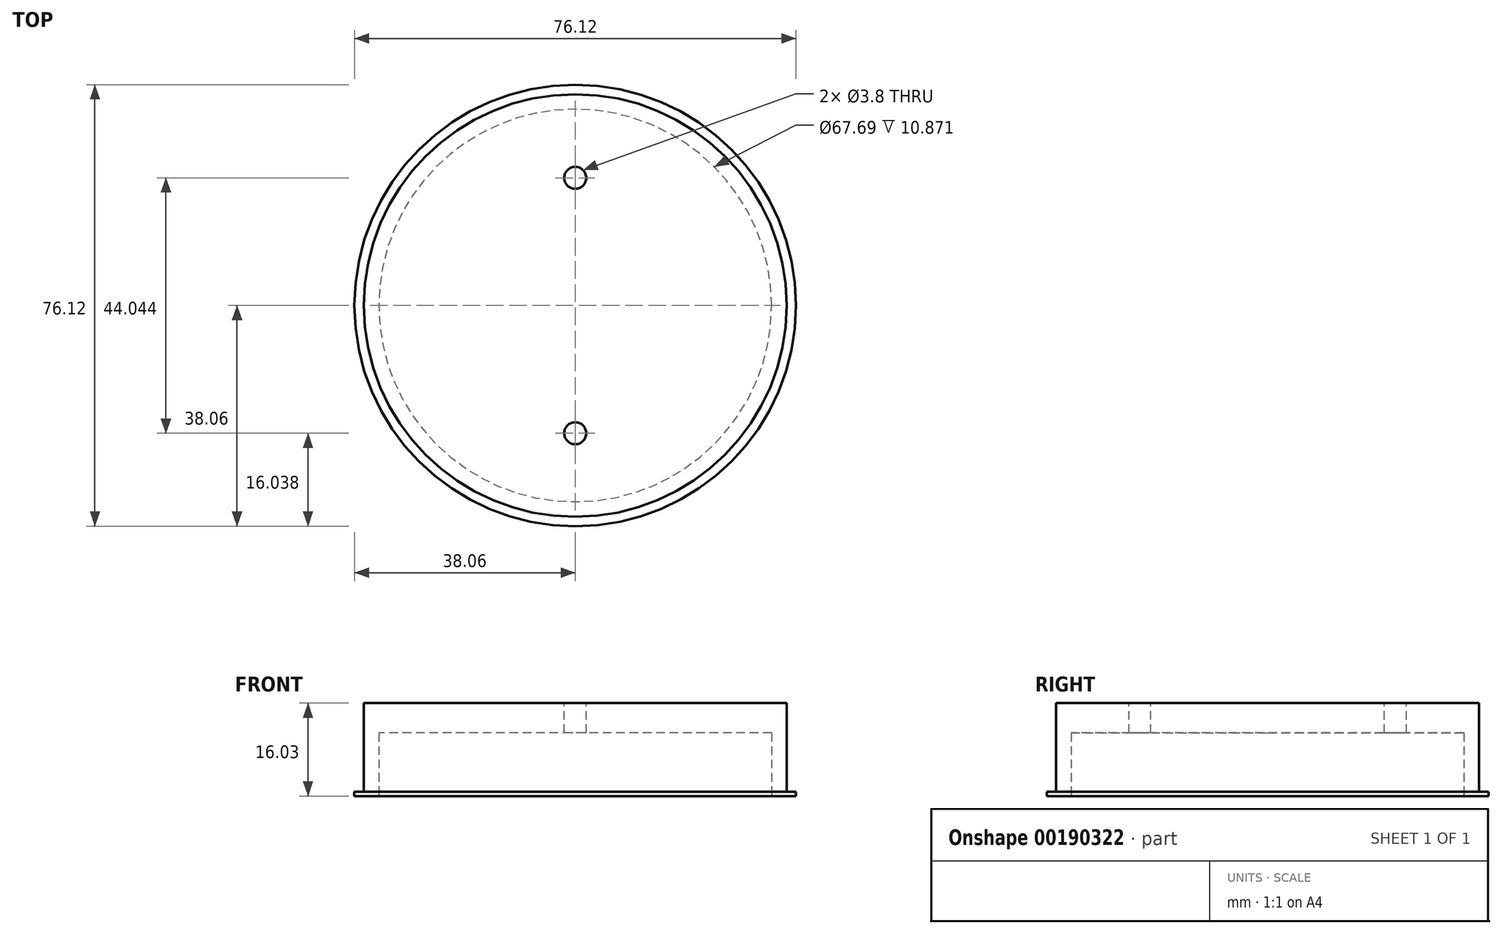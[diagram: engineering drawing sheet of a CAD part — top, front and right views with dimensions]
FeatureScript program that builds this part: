
annotation { "Feature Type Name" : "Feature", "Feature Type Description" : "" }
export const myFeature = defineFeature(function(context is Context, id is Id, definition is map)
    precondition{}
    {
        {
            var Q0;
            Q0=qCreatedBy(makeId("Top.planeOp"),FACE);
            var sketch = newSketch(context, id + "F0", { "sketchPlane" : qUnion([Q0])});
            skCircle(sketch, "E0", {"center": v(0, 0) * mm, "radius": 38.06 * mm});
            skCircle(sketch, "E1", {"center": v(0, 0) * mm, "radius": 36.44 * mm});
            skCircle(sketch, "E2", {"center": v(0, 0) * mm, "radius": 33.85 * mm});
            skSolve(sketch);
        }
        {
            var Q0;
            Q0=makeQuery(id+"F0.imprint","IMPRINT",FACE,{"disambiguationData":[TD([[makeQuery(id+"F0.imprint","IMPRINT",EDGE,{"derivedFrom":sQuery(id+"F0.wireOp",EDGE,"E0")}),1.0]])]});
            extrude(context, id + "F1", {"entities" : qUnion([Q0]), "depth" : 0.71 * mm});
        }
        {
            var Q0;
            Q0=makeQuery(id+"F0.imprint","IMPRINT",FACE,{"disambiguationData":[TD([[makeQuery(id+"F0.imprint","IMPRINT",EDGE,{"derivedFrom":sQuery(id+"F0.wireOp",EDGE,"E1")}),1.0]])]});
            var Q1;
            Q1=makeQuery(id+"F0.imprint","IMPRINT",FACE,{"disambiguationData":[TD([[makeQuery(id+"F0.imprint","IMPRINT",EDGE,{"derivedFrom":sQuery(id+"F0.wireOp",EDGE,"E2")}),1.0]])]});
            extrude(context, id + "F2", {"entities" : qUnion([Q0, Q1]), "operationType" : NewBodyOperationType.ADD, "depth" : 16.03 * mm});
        }
        {
            var Q0;
            Q0=makeQuery(id+"F0.imprint","IMPRINT",FACE,{"disambiguationData":[TD([[makeQuery(id+"F0.imprint","IMPRINT",EDGE,{"derivedFrom":sQuery(id+"F0.wireOp",EDGE,"E2")}),1.0]])]});
            extrude(context, id + "F3", {"entities" : qUnion([Q0]), "operationType" : NewBodyOperationType.REMOVE, "depth" : 10.87 * mm});
        }
        {
            var Q0;
            Q0=makeQuery(id+"F0.imprint","IMPRINT",FACE,{"disambiguationData":[TD([[makeQuery(id+"F0.imprint","IMPRINT",EDGE,{"derivedFrom":sQuery(id+"F0.wireOp",EDGE,"E2")}),1.0]])]});
            var sketch = newSketch(context, id + "F4", { "sketchPlane" : qUnion([Q0])});
            skLineSegment(sketch, "E3", {"start": v(-6.96, -22.02) * mm, "end": v(11.6, -22.02) * mm});
            skLineSegment(sketch, "E4", {"start": v(-5.97, 22.02) * mm, "end": v(8.6, 22.02) * mm});
            skLineSegment(sketch, "E5", {"start": v(0, 0) * mm, "end": v(0, 22.02) * mm});
            skLineSegment(sketch, "E6", {"start": v(0, 0) * mm, "end": v(0, -22.02) * mm});
            skSolve(sketch);
        }
        {
            var Q0;
            Q0=sQuery(id+"F4.wireOp",VERTEX,"E6.end");
            var Q1;
            Q1=sQuery(id+"F4.wireOp",VERTEX,"E5.end");
            var Q2;
            Q2=makeQuery(id+"F1.opExtrude","SWEPT_BODY",BODY,{"disambiguationData":[OSD([sQuery(id+"F0.wireOp",EDGE,"E0"),sQuery(id+"F0.wireOp",EDGE,"E1")])]});
            hole(context, id + "F5", {"style" : HoleStyle.SIMPLE, "endStyle" : HoleEndStyle.THROUGH, "oppositeDirection" : true, "standardTappedOrClearance" : lookupTablePath({ "standard" : "ANSI", "fit" : "Normal (ASME)", "size" : "#6", "type" : "Clearance" }), "standardBlindInLast" : lookupTablePath({ "fit" : "Free", "standard" : "ANSI", "size" : "#6", "type" : "Clearance" }), "holeDiameter" : 3.8 * mm, "locations" : qUnion([Q0, Q1]), "scope" : qUnion([Q2]), "isTappedThrough" : true, "startStyle" : HoleStartStyle.PART});
        }
    });
